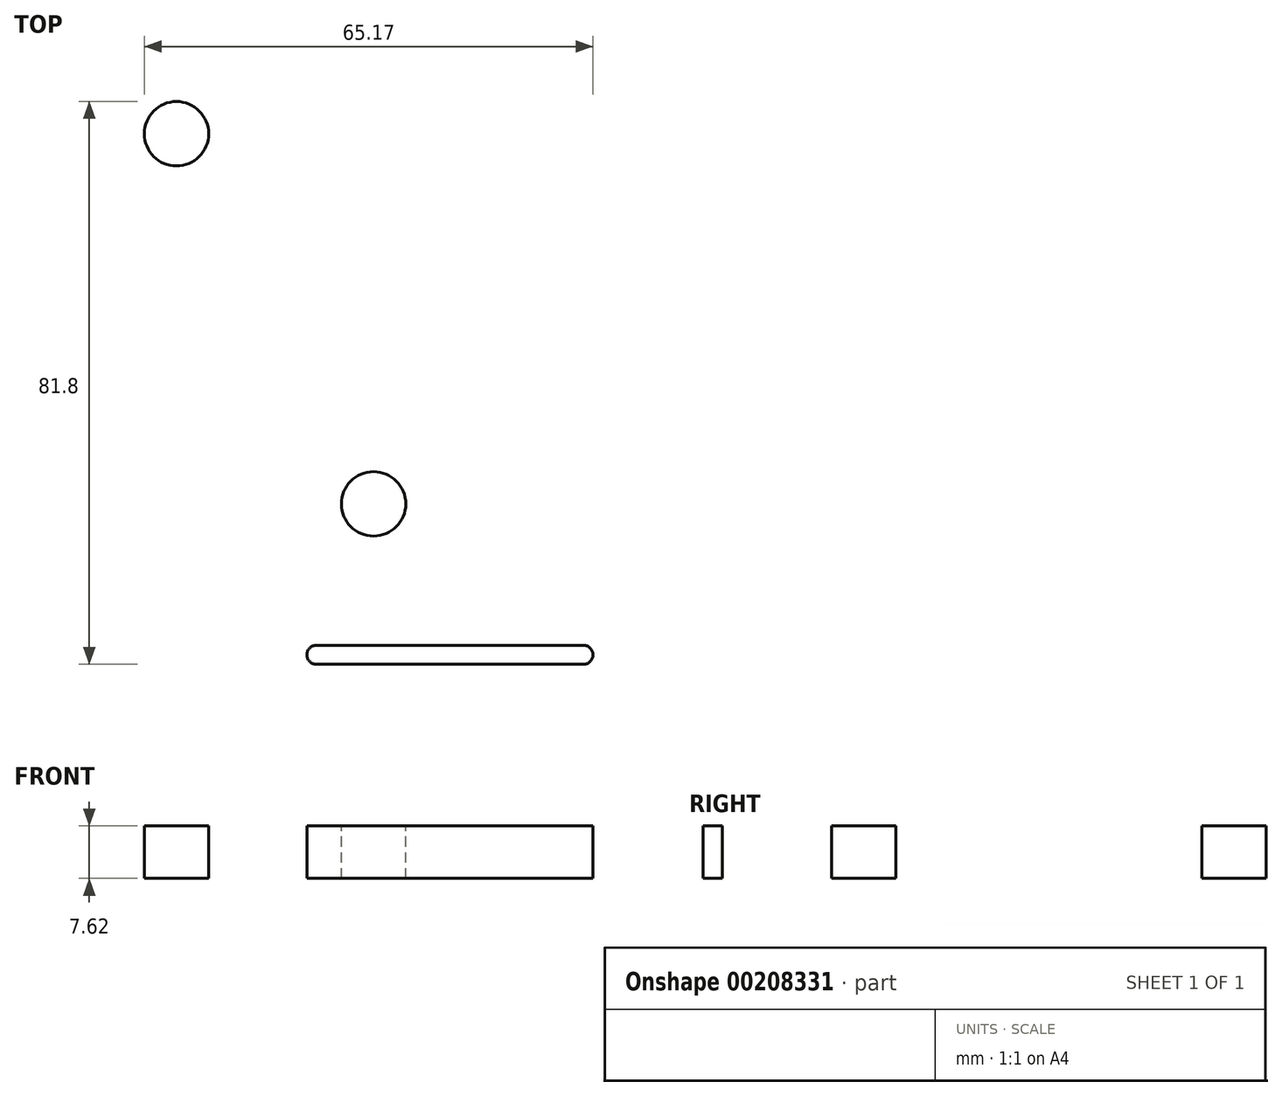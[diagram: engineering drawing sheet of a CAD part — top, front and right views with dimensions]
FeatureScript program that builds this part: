
annotation { "Feature Type Name" : "Feature", "Feature Type Description" : "" }
export const myFeature = defineFeature(function(context is Context, id is Id, definition is map)
    precondition{}
    {
        {
            var Q0;
            Q0=qCreatedBy(makeId("Top.planeOp"),FACE);
            var sketch = newSketch(context, id + "F0", { "sketchPlane" : qUnion([Q0])});
            skLineSegment(sketch, "E0.bottom", {"start": v(-60.27, 58.3) * mm, "end": v(60.27, 58.3) * mm});
            skLineSegment(sketch, "E0.top", {"start": v(-60.27, -58.3) * mm, "end": v(60.27, -58.3) * mm});
            skLineSegment(sketch, "E0.left", {"start": v(-60.27, 58.3) * mm, "end": v(-60.27, -58.3) * mm});
            skLineSegment(sketch, "E0.right", {"start": v(60.27, 58.3) * mm, "end": v(60.27, -58.3) * mm});
            skPoint(sketch, "E0.middle", {"position": v(0, 0) * mm});
            skSolve(sketch);
        }
        {
            var Q0;
            Q0=makeQuery(id+"F0.imprint","IMPRINT",FACE,{"disambiguationData":[TD([[makeQuery(id+"F0.imprint","IMPRINT",EDGE,{"derivedFrom":sQuery(id+"F0.wireOp",EDGE,"E0.bottom")}),-1.0]])]});
            extrude(context, id + "F1", {"entities" : qUnion([Q0]), "depth" : 7.62 * mm});
        }
        {
            var Q0;
            Q0=makeQuery(id+"F1.opExtrude","SWEPT_EDGE",EDGE,{"disambiguationData":[OSD([sQuery(id+"F0.wireOp",EDGE,"E0.top"),sQuery(id+"F0.wireOp",EDGE,"E0.right")])]});
            var Q1;
            Q1=makeQuery(id+"F1.opExtrude","SWEPT_EDGE",EDGE,{"disambiguationData":[OSD([sQuery(id+"F0.wireOp",EDGE,"E0.top"),sQuery(id+"F0.wireOp",EDGE,"E0.left")])]});
            var Q2;
            Q2=makeQuery(id+"F1.opExtrude","SWEPT_EDGE",EDGE,{"disambiguationData":[OSD([sQuery(id+"F0.wireOp",EDGE,"E0.bottom"),sQuery(id+"F0.wireOp",EDGE,"E0.left")])]});
            var Q3;
            Q3=makeQuery(id+"F1.opExtrude","SWEPT_EDGE",EDGE,{"disambiguationData":[OSD([sQuery(id+"F0.wireOp",EDGE,"E0.bottom"),sQuery(id+"F0.wireOp",EDGE,"E0.right")])]});
            fillet(context, id + "F2", {"entities" : qUnion([Q0, Q1, Q2, Q3]), "radius" : 5.08 * mm, "tangentPropagation" : true, "allowEdgeOverflow" : false});
        }
        {
            var Q0;
            Q0=makeQuery(id+"F1.opExtrude","CAP_FACE",FACE,{"disambiguationData":[OSD([sQuery(id+"F0.wireOp",EDGE,"E0.bottom"),sQuery(id+"F0.wireOp",EDGE,"E0.top"),sQuery(id+"F0.wireOp",EDGE,"E0.left"),sQuery(id+"F0.wireOp",EDGE,"E0.right")])],"isStart":false});
            var sketch = newSketch(context, id + "F3", { "sketchPlane" : qUnion([Q0])});
            skLineSegment(sketch, "E1.bottom", {"start": v(30.94, -10.74) * mm, "end": v(14.32, -10.74) * mm});
            skLineSegment(sketch, "E1.top", {"start": v(30.94, 10.74) * mm, "end": v(14.32, 10.74) * mm});
            skLineSegment(sketch, "E1.left", {"start": v(30.94, -10.74) * mm, "end": v(30.94, 10.74) * mm});
            skLineSegment(sketch, "E1.right", {"start": v(14.32, -10.74) * mm, "end": v(14.32, 10.74) * mm});
            skPoint(sketch, "E1.middle", {"position": v(22.63, 0) * mm});
            skCircle(sketch, "E2", {"center": v(14.32, 26.9) * mm, "radius": 4.68 * mm});
            skLineSegment(sketch, "E3.bottom", {"start": v(6, 50.22) * mm, "end": v(44.8, 50.22) * mm});
            skLineSegment(sketch, "E3.top", {"start": v(6, 47.45) * mm, "end": v(44.8, 47.45) * mm});
            skLineSegment(sketch, "E4.bottom", {"start": v(17.09, 43.56) * mm, "end": v(40.18, 43.56) * mm});
            skLineSegment(sketch, "E4.top", {"start": v(17.09, 40.8) * mm, "end": v(40.18, 40.8) * mm});
            skArc(sketch, "E5", {"start": v(6, 50.22) * mm, "mid": v(4.62, 48.84) * mm, "end": v(6, 47.45) * mm});
            skArc(sketch, "E6", {"start": v(44.8, 47.45) * mm, "mid": v(46.18, 48.84) * mm, "end": v(44.8, 50.22) * mm});
            skArc(sketch, "E7", {"start": v(17.09, 43.56) * mm, "mid": v(15.7, 42.18) * mm, "end": v(17.09, 40.8) * mm});
            skArc(sketch, "E8", {"start": v(40.18, 40.8) * mm, "mid": v(41.56, 42.18) * mm, "end": v(40.18, 43.56) * mm});
            skLineSegment(sketch, "E9.MirrorCS", {"start": v(-6, 50.22) * mm, "end": v(-44.8, 50.22) * mm});
            skLineSegment(sketch, "E10.MirrorCS", {"start": v(-6, 47.45) * mm, "end": v(-44.8, 47.45) * mm});
            skArc(sketch, "E11.MirrorCS", {"start": v(-6, 50.22) * mm, "mid": v(-4.62, 48.84) * mm, "end": v(-6, 47.45) * mm});
            skArc(sketch, "E12.MirrorCS", {"start": v(-44.8, 47.45) * mm, "mid": v(-46.18, 48.84) * mm, "end": v(-44.8, 50.22) * mm});
            skLineSegment(sketch, "E13.MirrorCS", {"start": v(-17.09, 43.56) * mm, "end": v(-40.18, 43.56) * mm});
            skLineSegment(sketch, "E14.MirrorCS", {"start": v(-17.09, 40.8) * mm, "end": v(-40.18, 40.8) * mm});
            skArc(sketch, "E15.MirrorCS", {"start": v(-17.09, 43.56) * mm, "mid": v(-15.7, 42.18) * mm, "end": v(-17.09, 40.8) * mm});
            skArc(sketch, "E16.MirrorCS", {"start": v(-40.18, 40.8) * mm, "mid": v(-41.56, 42.18) * mm, "end": v(-40.18, 43.56) * mm});
            skLineSegment(sketch, "E17.MirrorCS", {"start": v(-30.94, -10.74) * mm, "end": v(-30.94, 10.74) * mm});
            skLineSegment(sketch, "E18.MirrorCS", {"start": v(-30.94, 10.74) * mm, "end": v(-14.32, 10.74) * mm});
            skLineSegment(sketch, "E19.MirrorCS", {"start": v(-14.32, -10.74) * mm, "end": v(-14.32, 10.74) * mm});
            skLineSegment(sketch, "E20.MirrorCS", {"start": v(-30.94, -10.74) * mm, "end": v(-14.32, -10.74) * mm});
            skCircle(sketch, "E21.MirrorC", {"center": v(-14.32, 26.9) * mm, "radius": 4.68 * mm});
            skCircle(sketch, "E22.MirrorC", {"center": v(-14.32, -26.9) * mm, "radius": 4.68 * mm});
            skCircle(sketch, "E23.MirrorC", {"center": v(14.32, -26.9) * mm, "radius": 4.68 * mm});
            skLineSegment(sketch, "E24.MirrorCS", {"start": v(17.09, -43.56) * mm, "end": v(40.18, -43.56) * mm});
            skLineSegment(sketch, "E25.MirrorCS", {"start": v(17.09, -40.8) * mm, "end": v(40.18, -40.8) * mm});
            skArc(sketch, "E26.MirrorCS", {"start": v(17.09, -43.56) * mm, "mid": v(15.7, -42.18) * mm, "end": v(17.09, -40.8) * mm});
            skArc(sketch, "E27.MirrorCS", {"start": v(40.18, -40.8) * mm, "mid": v(41.56, -42.18) * mm, "end": v(40.18, -43.56) * mm});
            skArc(sketch, "E28.MirrorCS", {"start": v(6, -50.22) * mm, "mid": v(4.62, -48.84) * mm, "end": v(6, -47.45) * mm});
            skArc(sketch, "E29.MirrorCS", {"start": v(44.8, -47.45) * mm, "mid": v(46.18, -48.84) * mm, "end": v(44.8, -50.22) * mm});
            skLineSegment(sketch, "E30.MirrorCS", {"start": v(6, -47.45) * mm, "end": v(44.8, -47.45) * mm});
            skLineSegment(sketch, "E31.MirrorCS", {"start": v(6, -50.22) * mm, "end": v(44.8, -50.22) * mm});
            skLineSegment(sketch, "E32.MirrorCS", {"start": v(-17.09, -40.8) * mm, "end": v(-40.18, -40.8) * mm});
            skLineSegment(sketch, "E33.MirrorCS", {"start": v(-17.09, -43.56) * mm, "end": v(-40.18, -43.56) * mm});
            skArc(sketch, "E34.MirrorCS", {"start": v(-17.09, -43.56) * mm, "mid": v(-15.7, -42.18) * mm, "end": v(-17.09, -40.8) * mm});
            skArc(sketch, "E35.MirrorCS", {"start": v(-40.18, -40.8) * mm, "mid": v(-41.56, -42.18) * mm, "end": v(-40.18, -43.56) * mm});
            skLineSegment(sketch, "E36.MirrorCS", {"start": v(-6, -47.45) * mm, "end": v(-44.8, -47.45) * mm});
            skLineSegment(sketch, "E37.MirrorCS", {"start": v(-6, -50.22) * mm, "end": v(-44.8, -50.22) * mm});
            skArc(sketch, "E38.MirrorCS", {"start": v(-6, -50.22) * mm, "mid": v(-4.62, -48.84) * mm, "end": v(-6, -47.45) * mm});
            skArc(sketch, "E39.MirrorCS", {"start": v(-44.8, -47.45) * mm, "mid": v(-46.18, -48.84) * mm, "end": v(-44.8, -50.22) * mm});
            skSolve(sketch);
        }
        {
            var Q0;
            Q0=makeQuery(id+"F3.imprint","IMPRINT",FACE,{"disambiguationData":[TD([[makeQuery(id+"F3.imprint","IMPRINT",EDGE,{"derivedFrom":sQuery(id+"F3.wireOp",EDGE,"E17.MirrorCS")}),-1.0]])]});
            var Q1;
            Q1=makeQuery(id+"F3.imprint","IMPRINT",FACE,{"disambiguationData":[TD([[makeQuery(id+"F3.imprint","IMPRINT",EDGE,{"derivedFrom":sQuery(id+"F3.wireOp",EDGE,"E1.bottom")}),-1.0]])]});
            var Q2;
            Q2=makeQuery(id+"F3.imprint","IMPRINT",FACE,{"disambiguationData":[TD([[makeQuery(id+"F3.imprint","IMPRINT",EDGE,{"derivedFrom":sQuery(id+"F3.wireOp",EDGE,"E21.MirrorC")}),-1.0]])]});
            var Q3;
            Q3=makeQuery(id+"F3.imprint","IMPRINT",FACE,{"disambiguationData":[TD([[makeQuery(id+"F3.imprint","IMPRINT",EDGE,{"derivedFrom":sQuery(id+"F3.wireOp",EDGE,"E4.bottom")}),-1.0]])]});
            var Q4;
            Q4=makeQuery(id+"F3.imprint","IMPRINT",FACE,{"disambiguationData":[TD([[makeQuery(id+"F3.imprint","IMPRINT",EDGE,{"derivedFrom":sQuery(id+"F3.wireOp",EDGE,"E3.bottom")}),-1.0]])]});
            var Q5;
            Q5=makeQuery(id+"F3.imprint","IMPRINT",FACE,{"disambiguationData":[TD([[makeQuery(id+"F3.imprint","IMPRINT",EDGE,{"derivedFrom":sQuery(id+"F3.wireOp",EDGE,"E9.MirrorCS")}),1.0]])]});
            var Q6;
            Q6=makeQuery(id+"F3.imprint","IMPRINT",FACE,{"disambiguationData":[TD([[makeQuery(id+"F3.imprint","IMPRINT",EDGE,{"derivedFrom":sQuery(id+"F3.wireOp",EDGE,"E13.MirrorCS")}),1.0]])]});
            var Q7;
            Q7=makeQuery(id+"F3.imprint","IMPRINT",FACE,{"disambiguationData":[TD([[makeQuery(id+"F3.imprint","IMPRINT",EDGE,{"derivedFrom":sQuery(id+"F3.wireOp",EDGE,"E24.MirrorCS")}),1.0]])]});
            var Q8;
            Q8=makeQuery(id+"F3.imprint","IMPRINT",FACE,{"disambiguationData":[TD([[makeQuery(id+"F3.imprint","IMPRINT",EDGE,{"derivedFrom":sQuery(id+"F3.wireOp",EDGE,"E32.MirrorCS")}),1.0]])]});
            var Q9;
            Q9=makeQuery(id+"F3.imprint","IMPRINT",FACE,{"disambiguationData":[TD([[makeQuery(id+"F3.imprint","IMPRINT",EDGE,{"derivedFrom":sQuery(id+"F3.wireOp",EDGE,"E36.MirrorCS")}),1.0]])]});
            var Q10;
            Q10=makeQuery(id+"F3.imprint","IMPRINT",FACE,{"disambiguationData":[TD([[makeQuery(id+"F3.imprint","IMPRINT",EDGE,{"derivedFrom":sQuery(id+"F3.wireOp",EDGE,"E28.MirrorCS")}),-1.0]])]});
            var Q11;
            Q11=makeQuery(id+"F3.imprint","IMPRINT",FACE,{"disambiguationData":[TD([[makeQuery(id+"F3.imprint","IMPRINT",EDGE,{"derivedFrom":sQuery(id+"F3.wireOp",EDGE,"E22.MirrorC")}),1.0]])]});
            var Q12;
            Q12=makeQuery(id+"F3.imprint","IMPRINT",FACE,{"disambiguationData":[TD([[makeQuery(id+"F3.imprint","IMPRINT",EDGE,{"derivedFrom":sQuery(id+"F3.wireOp",EDGE,"E23.MirrorC")}),-1.0]])]});
            var Q13;
            Q13=makeQuery(id+"F3.imprint","IMPRINT",FACE,{"disambiguationData":[TD([[makeQuery(id+"F3.imprint","IMPRINT",EDGE,{"derivedFrom":sQuery(id+"F3.wireOp",EDGE,"E2")}),1.0]])]});
            extrude(context, id + "F4", {"entities" : qUnion([Q0, Q1, Q2, Q3, Q4, Q5, Q6, Q7, Q8, Q9, Q10, Q11, Q12, Q13]), "operationType" : NewBodyOperationType.REMOVE, "oppositeDirection" : true, "depth" : 25.4 * mm});
        }
    });
